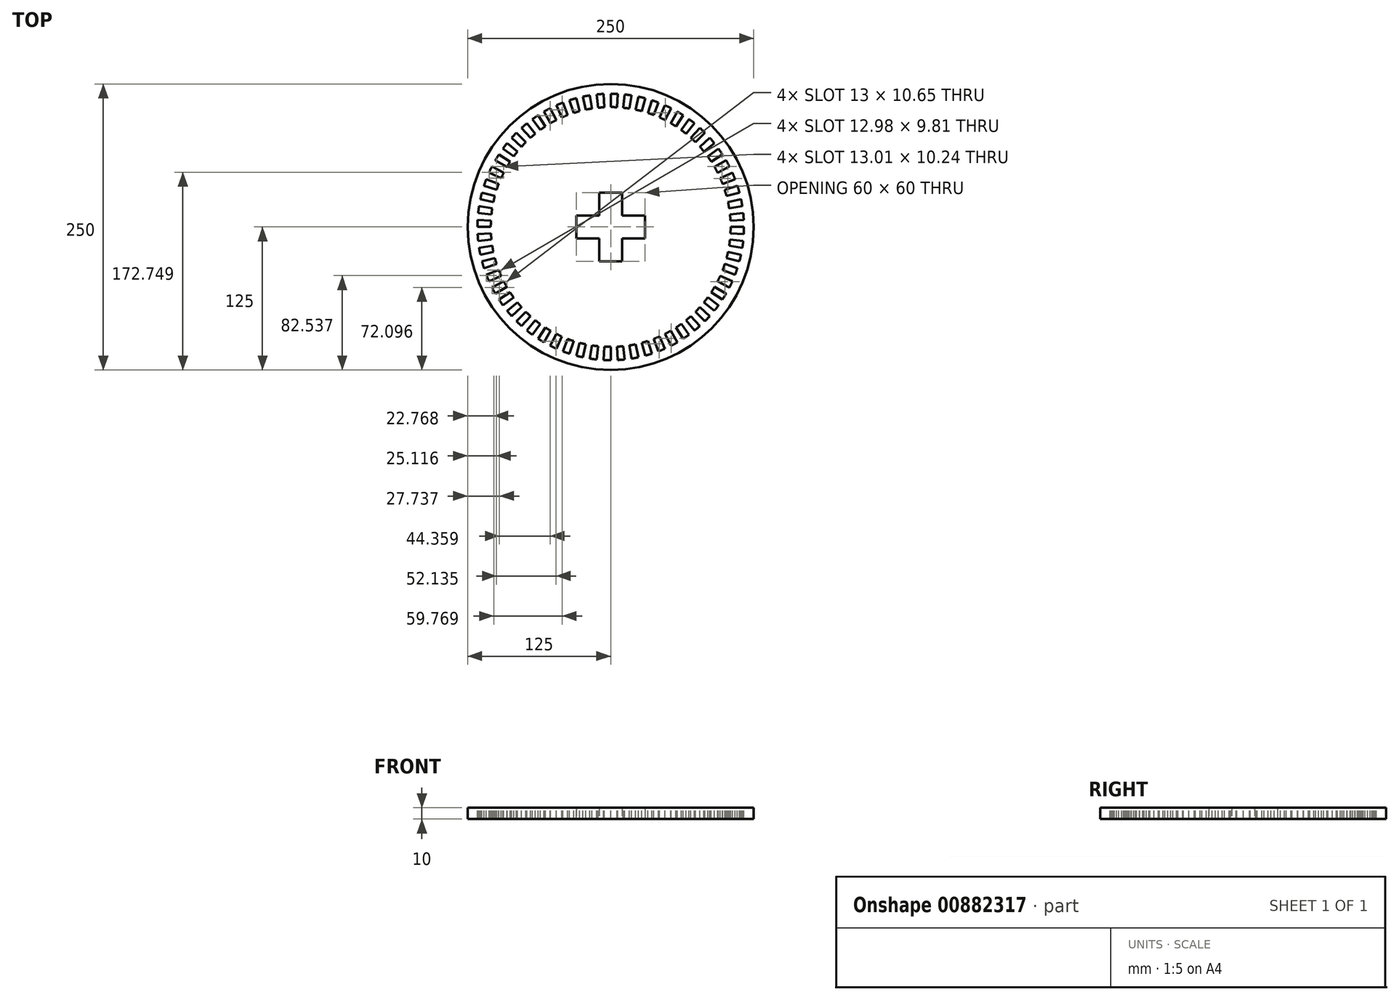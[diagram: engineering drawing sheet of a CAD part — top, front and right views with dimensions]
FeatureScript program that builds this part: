
annotation { "Feature Type Name" : "Feature", "Feature Type Description" : "" }
export const myFeature = defineFeature(function(context is Context, id is Id, definition is map)
    precondition{}
    {
        {
            var Q0;
            Q0=qCreatedBy(makeId("Top.planeOp"),FACE);
            var sketch = newSketch(context, id + "F0", { "sketchPlane" : qUnion([Q0])});
            skCircle(sketch, "E0", {"center": v(0, 0) * mm, "radius": 145 * mm});
            skArc(sketch, "E1", {"start": v(9.54, 136.41) * mm, "mid": v(4.77, 136.66) * mm, "end": v(0, 136.75) * mm});
            skArc(sketch, "E2", {"start": v(8, 114.55) * mm, "mid": v(4, 114.76) * mm, "end": v(0, 114.83) * mm});
            skLineSegment(sketch, "E3", {"start": v(0, 0) * mm, "end": v(0, 38.61) * mm, "construction": true});
            skLineSegment(sketch, "E4", {"start": v(0, 38.61) * mm, "end": v(0, 0) * mm, "construction": true});
            skLineSegment(sketch, "E5", {"start": v(0, 0) * mm, "end": v(-47.77, 0) * mm, "construction": true});
            skLineSegment(sketch, "E6", {"start": v(0, 30) * mm, "end": v(-10, 30) * mm});
            skLineSegment(sketch, "E7", {"start": v(-10, 30) * mm, "end": v(-10, 10) * mm});
            skLineSegment(sketch, "E8", {"start": v(-10, 10) * mm, "end": v(-30, 10) * mm});
            skLineSegment(sketch, "E9", {"start": v(-30, 10) * mm, "end": v(-30, 0) * mm});
            skLineSegment(sketch, "E10.MirrorCS", {"start": v(-30, -10) * mm, "end": v(-30, 0) * mm});
            skLineSegment(sketch, "E11.MirrorCS", {"start": v(-10, -10) * mm, "end": v(-30, -10) * mm});
            skLineSegment(sketch, "E12.MirrorCS", {"start": v(-10, -30) * mm, "end": v(-10, -10) * mm});
            skLineSegment(sketch, "E13.MirrorCS", {"start": v(0, -30) * mm, "end": v(-10, -30) * mm});
            skLineSegment(sketch, "E14.MirrorCS", {"start": v(0, 30) * mm, "end": v(10, 30) * mm});
            skLineSegment(sketch, "E15.MirrorCS", {"start": v(10, 30) * mm, "end": v(10, 10) * mm});
            skLineSegment(sketch, "E16.MirrorCS", {"start": v(10, 10) * mm, "end": v(30, 10) * mm});
            skLineSegment(sketch, "E17.MirrorCS", {"start": v(30, 10) * mm, "end": v(30, 0) * mm});
            skLineSegment(sketch, "E18.MirrorCS", {"start": v(30, -10) * mm, "end": v(30, 0) * mm});
            skLineSegment(sketch, "E19.MirrorCS", {"start": v(10, -10) * mm, "end": v(30, -10) * mm});
            skLineSegment(sketch, "E20.MirrorCS", {"start": v(0, -30) * mm, "end": v(10, -30) * mm});
            skLineSegment(sketch, "E21.MirrorCS", {"start": v(10, -30) * mm, "end": v(10, -10) * mm});
            skLineSegment(sketch, "E22", {"start": v(0, 114.83) * mm, "end": v(0, 136.75) * mm});
            skLineSegment(sketch, "E23", {"start": v(8, 114.55) * mm, "end": v(9.54, 136.41) * mm});
            skArc(sketch, "E24.1.0", {"start": v(-10, 114.4) * mm, "mid": v(-14, 113.98) * mm, "end": v(-17.96, 113.42) * mm});
            skLineSegment(sketch, "E24.1.1", {"start": v(-17.96, 113.42) * mm, "end": v(-21.4, 135.06) * mm});
            skArc(sketch, "E24.1.2", {"start": v(-11.92, 136.23) * mm, "mid": v(-16.67, 135.73) * mm, "end": v(-21.4, 135.06) * mm});
            skLineSegment(sketch, "E24.1.3", {"start": v(-10, 114.4) * mm, "end": v(-11.92, 136.23) * mm});
            skArc(sketch, "E24.2.0", {"start": v(-27.78, 111.42) * mm, "mid": v(-31.65, 110.39) * mm, "end": v(-35.49, 109.21) * mm});
            skLineSegment(sketch, "E24.2.1", {"start": v(-35.49, 109.21) * mm, "end": v(-42.26, 130.05) * mm});
            skArc(sketch, "E24.2.2", {"start": v(-33.08, 132.68) * mm, "mid": v(-37.7, 131.45) * mm, "end": v(-42.26, 130.05) * mm});
            skLineSegment(sketch, "E24.2.3", {"start": v(-27.78, 111.42) * mm, "end": v(-33.08, 132.68) * mm});
            skArc(sketch, "E24.3.0", {"start": v(-44.87, 105.7) * mm, "mid": v(-48.53, 104.07) * mm, "end": v(-52.13, 102.32) * mm});
            skLineSegment(sketch, "E24.3.1", {"start": v(-52.13, 102.32) * mm, "end": v(-62.08, 121.84) * mm});
            skArc(sketch, "E24.3.2", {"start": v(-53.43, 125.88) * mm, "mid": v(-57.8, 123.93) * mm, "end": v(-62.08, 121.84) * mm});
            skLineSegment(sketch, "E24.3.3", {"start": v(-44.87, 105.7) * mm, "end": v(-53.43, 125.88) * mm});
            skArc(sketch, "E24.4.0", {"start": v(-60.85, 97.38) * mm, "mid": v(-64.21, 95.2) * mm, "end": v(-67.5, 92.9) * mm});
            skLineSegment(sketch, "E24.4.1", {"start": v(-67.5, 92.9) * mm, "end": v(-80.38, 110.63) * mm});
            skArc(sketch, "E24.4.2", {"start": v(-72.47, 115.97) * mm, "mid": v(-76.47, 113.37) * mm, "end": v(-80.38, 110.63) * mm});
            skLineSegment(sketch, "E24.4.3", {"start": v(-60.85, 97.38) * mm, "end": v(-72.47, 115.97) * mm});
            skArc(sketch, "E24.5.0", {"start": v(-75.34, 86.67) * mm, "mid": v(-78.32, 83.98) * mm, "end": v(-81.2, 81.2) * mm});
            skLineSegment(sketch, "E24.5.1", {"start": v(-81.2, 81.2) * mm, "end": v(-96.7, 96.7) * mm});
            skArc(sketch, "E24.5.2", {"start": v(-89.71, 103.2) * mm, "mid": v(-93.26, 100.01) * mm, "end": v(-96.7, 96.7) * mm});
            skLineSegment(sketch, "E24.5.3", {"start": v(-75.34, 86.67) * mm, "end": v(-89.71, 103.2) * mm});
            skArc(sketch, "E24.6.0", {"start": v(-87.97, 73.81) * mm, "mid": v(-90.5, 70.7) * mm, "end": v(-92.9, 67.5) * mm});
            skLineSegment(sketch, "E24.6.1", {"start": v(-92.9, 67.5) * mm, "end": v(-110.63, 80.38) * mm});
            skArc(sketch, "E24.6.2", {"start": v(-104.75, 87.9) * mm, "mid": v(-107.76, 84.19) * mm, "end": v(-110.63, 80.38) * mm});
            skLineSegment(sketch, "E24.6.3", {"start": v(-87.97, 73.81) * mm, "end": v(-104.75, 87.9) * mm});
            skArc(sketch, "E24.7.0", {"start": v(-98.43, 59.14) * mm, "mid": v(-100.44, 55.67) * mm, "end": v(-102.32, 52.13) * mm});
            skLineSegment(sketch, "E24.7.1", {"start": v(-102.32, 52.13) * mm, "end": v(-121.84, 62.08) * mm});
            skArc(sketch, "E24.7.2", {"start": v(-117.22, 70.43) * mm, "mid": v(-119.6, 66.3) * mm, "end": v(-121.84, 62.08) * mm});
            skLineSegment(sketch, "E24.7.3", {"start": v(-98.43, 59.14) * mm, "end": v(-117.22, 70.43) * mm});
            skArc(sketch, "E24.8.0", {"start": v(-106.47, 43.02) * mm, "mid": v(-107.9, 39.28) * mm, "end": v(-109.21, 35.49) * mm});
            skLineSegment(sketch, "E24.8.1", {"start": v(-109.21, 35.49) * mm, "end": v(-130.05, 42.26) * mm});
            skArc(sketch, "E24.8.2", {"start": v(-126.79, 51.23) * mm, "mid": v(-128.5, 46.77) * mm, "end": v(-130.05, 42.26) * mm});
            skLineSegment(sketch, "E24.8.3", {"start": v(-106.47, 43.02) * mm, "end": v(-126.79, 51.23) * mm});
            skArc(sketch, "E24.9.0", {"start": v(-111.9, 25.83) * mm, "mid": v(-112.72, 21.91) * mm, "end": v(-113.42, 17.96) * mm});
            skLineSegment(sketch, "E24.9.1", {"start": v(-113.42, 17.96) * mm, "end": v(-135.06, 21.4) * mm});
            skArc(sketch, "E24.9.2", {"start": v(-133.24, 30.76) * mm, "mid": v(-134.23, 26.1) * mm, "end": v(-135.06, 21.4) * mm});
            skLineSegment(sketch, "E24.9.3", {"start": v(-111.9, 25.83) * mm, "end": v(-133.24, 30.76) * mm});
            skArc(sketch, "E24.10.0", {"start": v(-114.55, 8) * mm, "mid": v(-114.76, 4) * mm, "end": v(-114.83, 0) * mm});
            skLineSegment(sketch, "E24.10.1", {"start": v(-114.83, 0) * mm, "end": v(-136.75, 0) * mm});
            skArc(sketch, "E24.10.2", {"start": v(-136.41, 9.54) * mm, "mid": v(-136.66, 4.77) * mm, "end": v(-136.75, 0) * mm});
            skLineSegment(sketch, "E24.10.3", {"start": v(-114.55, 8) * mm, "end": v(-136.41, 9.54) * mm});
            skArc(sketch, "E24.11.0", {"start": v(-114.4, -10) * mm, "mid": v(-113.98, -14) * mm, "end": v(-113.42, -17.96) * mm});
            skLineSegment(sketch, "E24.11.1", {"start": v(-113.42, -17.96) * mm, "end": v(-135.06, -21.4) * mm});
            skArc(sketch, "E24.11.2", {"start": v(-136.23, -11.92) * mm, "mid": v(-135.73, -16.67) * mm, "end": v(-135.06, -21.4) * mm});
            skLineSegment(sketch, "E24.11.3", {"start": v(-114.4, -10) * mm, "end": v(-136.23, -11.92) * mm});
            skArc(sketch, "E24.12.0", {"start": v(-111.42, -27.78) * mm, "mid": v(-110.39, -31.65) * mm, "end": v(-109.21, -35.49) * mm});
            skLineSegment(sketch, "E24.12.1", {"start": v(-109.21, -35.49) * mm, "end": v(-130.05, -42.26) * mm});
            skArc(sketch, "E24.12.2", {"start": v(-132.68, -33.08) * mm, "mid": v(-131.45, -37.7) * mm, "end": v(-130.05, -42.26) * mm});
            skLineSegment(sketch, "E24.12.3", {"start": v(-111.42, -27.78) * mm, "end": v(-132.68, -33.08) * mm});
            skArc(sketch, "E24.13.0", {"start": v(-105.7, -44.87) * mm, "mid": v(-104.07, -48.53) * mm, "end": v(-102.32, -52.13) * mm});
            skLineSegment(sketch, "E24.13.1", {"start": v(-102.32, -52.13) * mm, "end": v(-121.84, -62.08) * mm});
            skArc(sketch, "E24.13.2", {"start": v(-125.88, -53.43) * mm, "mid": v(-123.93, -57.8) * mm, "end": v(-121.84, -62.08) * mm});
            skLineSegment(sketch, "E24.13.3", {"start": v(-105.7, -44.87) * mm, "end": v(-125.88, -53.43) * mm});
            skArc(sketch, "E24.14.0", {"start": v(-97.38, -60.85) * mm, "mid": v(-95.2, -64.21) * mm, "end": v(-92.9, -67.5) * mm});
            skLineSegment(sketch, "E24.14.1", {"start": v(-92.9, -67.5) * mm, "end": v(-110.63, -80.38) * mm});
            skArc(sketch, "E24.14.2", {"start": v(-115.97, -72.47) * mm, "mid": v(-113.37, -76.47) * mm, "end": v(-110.63, -80.38) * mm});
            skLineSegment(sketch, "E24.14.3", {"start": v(-97.38, -60.85) * mm, "end": v(-115.97, -72.47) * mm});
            skArc(sketch, "E24.15.0", {"start": v(-86.67, -75.34) * mm, "mid": v(-83.98, -78.32) * mm, "end": v(-81.2, -81.2) * mm});
            skLineSegment(sketch, "E24.15.1", {"start": v(-81.2, -81.2) * mm, "end": v(-96.7, -96.7) * mm});
            skArc(sketch, "E24.15.2", {"start": v(-103.2, -89.71) * mm, "mid": v(-100.01, -93.26) * mm, "end": v(-96.7, -96.7) * mm});
            skLineSegment(sketch, "E24.15.3", {"start": v(-86.67, -75.34) * mm, "end": v(-103.2, -89.71) * mm});
            skArc(sketch, "E24.16.0", {"start": v(-73.81, -87.97) * mm, "mid": v(-70.7, -90.5) * mm, "end": v(-67.5, -92.9) * mm});
            skLineSegment(sketch, "E24.16.1", {"start": v(-67.5, -92.9) * mm, "end": v(-80.38, -110.63) * mm});
            skArc(sketch, "E24.16.2", {"start": v(-87.9, -104.75) * mm, "mid": v(-84.19, -107.76) * mm, "end": v(-80.38, -110.63) * mm});
            skLineSegment(sketch, "E24.16.3", {"start": v(-73.81, -87.97) * mm, "end": v(-87.9, -104.75) * mm});
            skArc(sketch, "E24.17.0", {"start": v(-59.14, -98.43) * mm, "mid": v(-55.67, -100.44) * mm, "end": v(-52.13, -102.32) * mm});
            skLineSegment(sketch, "E24.17.1", {"start": v(-52.13, -102.32) * mm, "end": v(-62.08, -121.84) * mm});
            skArc(sketch, "E24.17.2", {"start": v(-70.43, -117.22) * mm, "mid": v(-66.3, -119.6) * mm, "end": v(-62.08, -121.84) * mm});
            skLineSegment(sketch, "E24.17.3", {"start": v(-59.14, -98.43) * mm, "end": v(-70.43, -117.22) * mm});
            skArc(sketch, "E24.18.0", {"start": v(-43.02, -106.47) * mm, "mid": v(-39.28, -107.9) * mm, "end": v(-35.49, -109.21) * mm});
            skLineSegment(sketch, "E24.18.1", {"start": v(-35.49, -109.21) * mm, "end": v(-42.26, -130.05) * mm});
            skArc(sketch, "E24.18.2", {"start": v(-51.23, -126.79) * mm, "mid": v(-46.77, -128.5) * mm, "end": v(-42.26, -130.05) * mm});
            skLineSegment(sketch, "E24.18.3", {"start": v(-43.02, -106.47) * mm, "end": v(-51.23, -126.79) * mm});
            skArc(sketch, "E24.19.0", {"start": v(-25.83, -111.9) * mm, "mid": v(-21.91, -112.72) * mm, "end": v(-17.96, -113.42) * mm});
            skLineSegment(sketch, "E24.19.1", {"start": v(-17.96, -113.42) * mm, "end": v(-21.4, -135.06) * mm});
            skArc(sketch, "E24.19.2", {"start": v(-30.76, -133.24) * mm, "mid": v(-26.1, -134.23) * mm, "end": v(-21.4, -135.06) * mm});
            skLineSegment(sketch, "E24.19.3", {"start": v(-25.83, -111.9) * mm, "end": v(-30.76, -133.24) * mm});
            skArc(sketch, "E24.20.0", {"start": v(-8, -114.55) * mm, "mid": v(-4, -114.76) * mm, "end": v(0, -114.83) * mm});
            skLineSegment(sketch, "E24.20.1", {"start": v(0, -114.83) * mm, "end": v(0, -136.75) * mm});
            skArc(sketch, "E24.20.2", {"start": v(-9.54, -136.41) * mm, "mid": v(-4.77, -136.66) * mm, "end": v(0, -136.75) * mm});
            skLineSegment(sketch, "E24.20.3", {"start": v(-8, -114.55) * mm, "end": v(-9.54, -136.41) * mm});
            skArc(sketch, "E24.21.0", {"start": v(10, -114.4) * mm, "mid": v(14, -113.98) * mm, "end": v(17.96, -113.42) * mm});
            skLineSegment(sketch, "E24.21.1", {"start": v(17.96, -113.42) * mm, "end": v(21.4, -135.06) * mm});
            skArc(sketch, "E24.21.2", {"start": v(11.92, -136.23) * mm, "mid": v(16.67, -135.73) * mm, "end": v(21.4, -135.06) * mm});
            skLineSegment(sketch, "E24.21.3", {"start": v(10, -114.4) * mm, "end": v(11.92, -136.23) * mm});
            skArc(sketch, "E24.22.0", {"start": v(27.78, -111.42) * mm, "mid": v(31.65, -110.39) * mm, "end": v(35.49, -109.21) * mm});
            skLineSegment(sketch, "E24.22.1", {"start": v(35.49, -109.21) * mm, "end": v(42.26, -130.05) * mm});
            skArc(sketch, "E24.22.2", {"start": v(33.08, -132.68) * mm, "mid": v(37.7, -131.45) * mm, "end": v(42.26, -130.05) * mm});
            skLineSegment(sketch, "E24.22.3", {"start": v(27.78, -111.42) * mm, "end": v(33.08, -132.68) * mm});
            skArc(sketch, "E24.23.0", {"start": v(44.87, -105.7) * mm, "mid": v(48.53, -104.07) * mm, "end": v(52.13, -102.32) * mm});
            skLineSegment(sketch, "E24.23.1", {"start": v(52.13, -102.32) * mm, "end": v(62.08, -121.84) * mm});
            skArc(sketch, "E24.23.2", {"start": v(53.43, -125.88) * mm, "mid": v(57.8, -123.93) * mm, "end": v(62.08, -121.84) * mm});
            skLineSegment(sketch, "E24.23.3", {"start": v(44.87, -105.7) * mm, "end": v(53.43, -125.88) * mm});
            skArc(sketch, "E24.24.0", {"start": v(60.85, -97.38) * mm, "mid": v(64.21, -95.2) * mm, "end": v(67.5, -92.9) * mm});
            skLineSegment(sketch, "E24.24.1", {"start": v(67.5, -92.9) * mm, "end": v(80.38, -110.63) * mm});
            skArc(sketch, "E24.24.2", {"start": v(72.47, -115.97) * mm, "mid": v(76.47, -113.37) * mm, "end": v(80.38, -110.63) * mm});
            skLineSegment(sketch, "E24.24.3", {"start": v(60.85, -97.38) * mm, "end": v(72.47, -115.97) * mm});
            skArc(sketch, "E24.25.0", {"start": v(75.34, -86.67) * mm, "mid": v(78.32, -83.98) * mm, "end": v(81.2, -81.2) * mm});
            skLineSegment(sketch, "E24.25.1", {"start": v(81.2, -81.2) * mm, "end": v(96.7, -96.7) * mm});
            skArc(sketch, "E24.25.2", {"start": v(89.71, -103.2) * mm, "mid": v(93.26, -100.01) * mm, "end": v(96.7, -96.7) * mm});
            skLineSegment(sketch, "E24.25.3", {"start": v(75.34, -86.67) * mm, "end": v(89.71, -103.2) * mm});
            skArc(sketch, "E24.26.0", {"start": v(87.97, -73.81) * mm, "mid": v(90.5, -70.7) * mm, "end": v(92.9, -67.5) * mm});
            skLineSegment(sketch, "E24.26.1", {"start": v(92.9, -67.5) * mm, "end": v(110.63, -80.38) * mm});
            skArc(sketch, "E24.26.2", {"start": v(104.75, -87.9) * mm, "mid": v(107.76, -84.19) * mm, "end": v(110.63, -80.38) * mm});
            skLineSegment(sketch, "E24.26.3", {"start": v(87.97, -73.81) * mm, "end": v(104.75, -87.9) * mm});
            skArc(sketch, "E24.27.0", {"start": v(98.43, -59.14) * mm, "mid": v(100.44, -55.67) * mm, "end": v(102.32, -52.13) * mm});
            skLineSegment(sketch, "E24.27.1", {"start": v(102.32, -52.13) * mm, "end": v(121.84, -62.08) * mm});
            skArc(sketch, "E24.27.2", {"start": v(117.22, -70.43) * mm, "mid": v(119.6, -66.3) * mm, "end": v(121.84, -62.08) * mm});
            skLineSegment(sketch, "E24.27.3", {"start": v(98.43, -59.14) * mm, "end": v(117.22, -70.43) * mm});
            skArc(sketch, "E24.28.0", {"start": v(106.47, -43.02) * mm, "mid": v(107.9, -39.28) * mm, "end": v(109.21, -35.49) * mm});
            skLineSegment(sketch, "E24.28.1", {"start": v(109.21, -35.49) * mm, "end": v(130.05, -42.26) * mm});
            skArc(sketch, "E24.28.2", {"start": v(126.79, -51.23) * mm, "mid": v(128.5, -46.77) * mm, "end": v(130.05, -42.26) * mm});
            skLineSegment(sketch, "E24.28.3", {"start": v(106.47, -43.02) * mm, "end": v(126.79, -51.23) * mm});
            skArc(sketch, "E24.29.0", {"start": v(111.9, -25.83) * mm, "mid": v(112.72, -21.91) * mm, "end": v(113.42, -17.96) * mm});
            skLineSegment(sketch, "E24.29.1", {"start": v(113.42, -17.96) * mm, "end": v(135.06, -21.4) * mm});
            skArc(sketch, "E24.29.2", {"start": v(133.24, -30.76) * mm, "mid": v(134.23, -26.1) * mm, "end": v(135.06, -21.4) * mm});
            skLineSegment(sketch, "E24.29.3", {"start": v(111.9, -25.83) * mm, "end": v(133.24, -30.76) * mm});
            skArc(sketch, "E24.30.0", {"start": v(114.55, -8) * mm, "mid": v(114.76, -4) * mm, "end": v(114.83, 0) * mm});
            skLineSegment(sketch, "E24.30.1", {"start": v(114.83, 0) * mm, "end": v(136.75, 0) * mm});
            skArc(sketch, "E24.30.2", {"start": v(136.41, -9.54) * mm, "mid": v(136.66, -4.77) * mm, "end": v(136.75, 0) * mm});
            skLineSegment(sketch, "E24.30.3", {"start": v(114.55, -8) * mm, "end": v(136.41, -9.54) * mm});
            skArc(sketch, "E24.31.0", {"start": v(114.4, 10) * mm, "mid": v(113.98, 14) * mm, "end": v(113.42, 17.96) * mm});
            skLineSegment(sketch, "E24.31.1", {"start": v(113.42, 17.96) * mm, "end": v(135.06, 21.4) * mm});
            skArc(sketch, "E24.31.2", {"start": v(136.23, 11.92) * mm, "mid": v(135.73, 16.67) * mm, "end": v(135.06, 21.4) * mm});
            skLineSegment(sketch, "E24.31.3", {"start": v(114.4, 10) * mm, "end": v(136.23, 11.92) * mm});
            skArc(sketch, "E24.32.0", {"start": v(111.42, 27.78) * mm, "mid": v(110.39, 31.65) * mm, "end": v(109.21, 35.49) * mm});
            skLineSegment(sketch, "E24.32.1", {"start": v(109.21, 35.49) * mm, "end": v(130.05, 42.26) * mm});
            skArc(sketch, "E24.32.2", {"start": v(132.68, 33.08) * mm, "mid": v(131.45, 37.7) * mm, "end": v(130.05, 42.26) * mm});
            skLineSegment(sketch, "E24.32.3", {"start": v(111.42, 27.78) * mm, "end": v(132.68, 33.08) * mm});
            skArc(sketch, "E24.33.0", {"start": v(105.7, 44.87) * mm, "mid": v(104.07, 48.53) * mm, "end": v(102.32, 52.13) * mm});
            skLineSegment(sketch, "E24.33.1", {"start": v(102.32, 52.13) * mm, "end": v(121.84, 62.08) * mm});
            skArc(sketch, "E24.33.2", {"start": v(125.88, 53.43) * mm, "mid": v(123.93, 57.8) * mm, "end": v(121.84, 62.08) * mm});
            skLineSegment(sketch, "E24.33.3", {"start": v(105.7, 44.87) * mm, "end": v(125.88, 53.43) * mm});
            skArc(sketch, "E24.34.0", {"start": v(97.38, 60.85) * mm, "mid": v(95.2, 64.21) * mm, "end": v(92.9, 67.5) * mm});
            skLineSegment(sketch, "E24.34.1", {"start": v(92.9, 67.5) * mm, "end": v(110.63, 80.38) * mm});
            skArc(sketch, "E24.34.2", {"start": v(115.97, 72.47) * mm, "mid": v(113.37, 76.47) * mm, "end": v(110.63, 80.38) * mm});
            skLineSegment(sketch, "E24.34.3", {"start": v(97.38, 60.85) * mm, "end": v(115.97, 72.47) * mm});
            skArc(sketch, "E24.35.0", {"start": v(86.67, 75.34) * mm, "mid": v(83.98, 78.32) * mm, "end": v(81.2, 81.2) * mm});
            skLineSegment(sketch, "E24.35.1", {"start": v(81.2, 81.2) * mm, "end": v(96.7, 96.7) * mm});
            skArc(sketch, "E24.35.2", {"start": v(103.2, 89.71) * mm, "mid": v(100.01, 93.26) * mm, "end": v(96.7, 96.7) * mm});
            skLineSegment(sketch, "E24.35.3", {"start": v(86.67, 75.34) * mm, "end": v(103.2, 89.71) * mm});
            skArc(sketch, "E24.36.0", {"start": v(73.81, 87.97) * mm, "mid": v(70.7, 90.5) * mm, "end": v(67.5, 92.9) * mm});
            skLineSegment(sketch, "E24.36.1", {"start": v(67.5, 92.9) * mm, "end": v(80.38, 110.63) * mm});
            skArc(sketch, "E24.36.2", {"start": v(87.9, 104.75) * mm, "mid": v(84.19, 107.76) * mm, "end": v(80.38, 110.63) * mm});
            skLineSegment(sketch, "E24.36.3", {"start": v(73.81, 87.97) * mm, "end": v(87.9, 104.75) * mm});
            skArc(sketch, "E24.37.0", {"start": v(59.14, 98.43) * mm, "mid": v(55.67, 100.44) * mm, "end": v(52.13, 102.32) * mm});
            skLineSegment(sketch, "E24.37.1", {"start": v(52.13, 102.32) * mm, "end": v(62.08, 121.84) * mm});
            skArc(sketch, "E24.37.2", {"start": v(70.43, 117.22) * mm, "mid": v(66.3, 119.6) * mm, "end": v(62.08, 121.84) * mm});
            skLineSegment(sketch, "E24.37.3", {"start": v(59.14, 98.43) * mm, "end": v(70.43, 117.22) * mm});
            skArc(sketch, "E24.38.0", {"start": v(43.02, 106.47) * mm, "mid": v(39.28, 107.9) * mm, "end": v(35.49, 109.21) * mm});
            skLineSegment(sketch, "E24.38.1", {"start": v(35.49, 109.21) * mm, "end": v(42.26, 130.05) * mm});
            skArc(sketch, "E24.38.2", {"start": v(51.23, 126.79) * mm, "mid": v(46.77, 128.5) * mm, "end": v(42.26, 130.05) * mm});
            skLineSegment(sketch, "E24.38.3", {"start": v(43.02, 106.47) * mm, "end": v(51.23, 126.79) * mm});
            skArc(sketch, "E24.39.0", {"start": v(25.83, 111.9) * mm, "mid": v(21.91, 112.72) * mm, "end": v(17.96, 113.42) * mm});
            skLineSegment(sketch, "E24.39.1", {"start": v(17.96, 113.42) * mm, "end": v(21.4, 135.06) * mm});
            skArc(sketch, "E24.39.2", {"start": v(30.76, 133.24) * mm, "mid": v(26.1, 134.23) * mm, "end": v(21.4, 135.06) * mm});
            skLineSegment(sketch, "E24.39.3", {"start": v(25.83, 111.9) * mm, "end": v(30.76, 133.24) * mm});
            skCircle(sketch, "E25", {"center": v(0, 0) * mm, "radius": 50 * mm});
            skSolve(sketch);
        }
        {
            var Q0;
            Q0=makeQuery(id+"F0.imprint","IMPRINT",FACE,{"disambiguationData":[TD([[makeQuery(id+"F0.imprint","IMPRINT",EDGE,{"derivedFrom":sQuery(id+"F0.wireOp",EDGE,"E6")}),-1.0]])]});
            extrude(context, id + "F1", {"entities" : qUnion([Q0]), "depth" : 10 * mm, "offsetDistance" : 25 * mm});
        }
        {
            var Q0;
            Q0=makeQuery(id+"F1.opExtrude","CAP_FACE",FACE,{"disambiguationData":[OSD([sQuery(id+"F0.wireOp",EDGE,"E6"),sQuery(id+"F0.wireOp",EDGE,"E7"),sQuery(id+"F0.wireOp",EDGE,"E8"),sQuery(id+"F0.wireOp",EDGE,"E9"),sQuery(id+"F0.wireOp",EDGE,"E10.MirrorCS"),sQuery(id+"F0.wireOp",EDGE,"E11.MirrorCS"),sQuery(id+"F0.wireOp",EDGE,"E12.MirrorCS"),sQuery(id+"F0.wireOp",EDGE,"E13.MirrorCS"),sQuery(id+"F0.wireOp",EDGE,"E14.MirrorCS"),sQuery(id+"F0.wireOp",EDGE,"E15.MirrorCS"),sQuery(id+"F0.wireOp",EDGE,"E16.MirrorCS"),sQuery(id+"F0.wireOp",EDGE,"E17.MirrorCS"),sQuery(id+"F0.wireOp",EDGE,"E18.MirrorCS"),sQuery(id+"F0.wireOp",EDGE,"E19.MirrorCS"),sQuery(id+"F0.wireOp",EDGE,"E20.MirrorCS"),sQuery(id+"F0.wireOp",EDGE,"E21.MirrorCS"),sQuery(id+"F0.wireOp",EDGE,"E25")])],"isStart":false});
            var sketch = newSketch(context, id + "F2", { "sketchPlane" : qUnion([Q0])});
            skCircle(sketch, "E26", {"center": v(0, 0) * mm, "radius": 125 * mm});
            skCircle(sketch, "E27", {"center": v(0, 0) * mm, "radius": 40.45 * mm});
            skSolve(sketch);
        }
        {
            var Q0;
            Q0=qSketchRegion(id+"F2",true);
            extrude(context, id + "F3", {"entities" : qUnion([Q0]), "operationType" : NewBodyOperationType.ADD, "oppositeDirection" : true, "depth" : 10 * mm, "offsetDistance" : 25 * mm});
        }
        {
            var Q0;
            Q0=makeQuery(id+"F3.boolean.opBoolean","MERGE",FACE,{"derivedFrom":[makeQuery(id+"F1.opExtrude","CAP_FACE",FACE,{"disambiguationData":[OSD([sQuery(id+"F0.wireOp",EDGE,"E6"),sQuery(id+"F0.wireOp",EDGE,"E7"),sQuery(id+"F0.wireOp",EDGE,"E8"),sQuery(id+"F0.wireOp",EDGE,"E9"),sQuery(id+"F0.wireOp",EDGE,"E10.MirrorCS"),sQuery(id+"F0.wireOp",EDGE,"E11.MirrorCS"),sQuery(id+"F0.wireOp",EDGE,"E12.MirrorCS"),sQuery(id+"F0.wireOp",EDGE,"E13.MirrorCS"),sQuery(id+"F0.wireOp",EDGE,"E14.MirrorCS"),sQuery(id+"F0.wireOp",EDGE,"E15.MirrorCS"),sQuery(id+"F0.wireOp",EDGE,"E16.MirrorCS"),sQuery(id+"F0.wireOp",EDGE,"E17.MirrorCS"),sQuery(id+"F0.wireOp",EDGE,"E18.MirrorCS"),sQuery(id+"F0.wireOp",EDGE,"E19.MirrorCS"),sQuery(id+"F0.wireOp",EDGE,"E20.MirrorCS"),sQuery(id+"F0.wireOp",EDGE,"E21.MirrorCS"),sQuery(id+"F0.wireOp",EDGE,"E25")])],"isStart":false}),makeQuery(id+"F3.opExtrude","CAP_FACE",FACE,{"disambiguationData":[OSD([sQuery(id+"F2.wireOp",EDGE,"E26"),sQuery(id+"F2.wireOp",EDGE,"E27")])],"isStart":true})]});
            var sketch = newSketch(context, id + "F4", { "sketchPlane" : qUnion([Q0])});
            skLineSegment(sketch, "E28", {"start": v(0, 104.8) * mm, "end": v(0, 116.46) * mm});
            skLineSegment(sketch, "E29", {"start": v(0, 116.46) * mm, "end": v(0, 104.8) * mm});
            skLineSegment(sketch, "E30", {"start": v(5.48, 104.66) * mm, "end": v(6.1, 116.3) * mm});
            skArc(sketch, "E31", {"start": v(6.1, 116.3) * mm, "mid": v(3.05, 116.42) * mm, "end": v(0, 116.46) * mm});
            skArc(sketch, "E32", {"start": v(5.48, 104.66) * mm, "mid": v(2.74, 104.77) * mm, "end": v(0, 104.8) * mm});
            skArc(sketch, "E33.1.0", {"start": v(-5.48, 104.66) * mm, "mid": v(-8.22, 104.48) * mm, "end": v(-10.95, 104.23) * mm});
            skLineSegment(sketch, "E33.1.1", {"start": v(-12.17, 115.82) * mm, "end": v(-10.95, 104.23) * mm});
            skArc(sketch, "E33.1.2", {"start": v(-6.1, 116.3) * mm, "mid": v(-9.14, 116.1) * mm, "end": v(-12.17, 115.82) * mm});
            skLineSegment(sketch, "E33.1.3", {"start": v(-5.48, 104.66) * mm, "end": v(-6.1, 116.3) * mm});
            skArc(sketch, "E33.2.0", {"start": v(-16.4, 103.51) * mm, "mid": v(-19.1, 103.05) * mm, "end": v(-21.79, 102.51) * mm});
            skLineSegment(sketch, "E33.2.1", {"start": v(-24.21, 113.91) * mm, "end": v(-21.79, 102.51) * mm});
            skArc(sketch, "E33.2.2", {"start": v(-18.22, 115.02) * mm, "mid": v(-21.22, 114.5) * mm, "end": v(-24.21, 113.91) * mm});
            skLineSegment(sketch, "E33.2.3", {"start": v(-16.4, 103.51) * mm, "end": v(-18.22, 115.02) * mm});
            skArc(sketch, "E33.3.0", {"start": v(-27.12, 101.23) * mm, "mid": v(-29.77, 100.49) * mm, "end": v(-32.39, 99.67) * mm});
            skLineSegment(sketch, "E33.3.1", {"start": v(-35.99, 110.76) * mm, "end": v(-32.39, 99.67) * mm});
            skArc(sketch, "E33.3.2", {"start": v(-30.14, 112.49) * mm, "mid": v(-33.08, 111.66) * mm, "end": v(-35.99, 110.76) * mm});
            skLineSegment(sketch, "E33.3.3", {"start": v(-27.12, 101.23) * mm, "end": v(-30.14, 112.49) * mm});
            skArc(sketch, "E33.4.0", {"start": v(-37.56, 97.84) * mm, "mid": v(-40.1, 96.83) * mm, "end": v(-42.63, 95.74) * mm});
            skLineSegment(sketch, "E33.4.1", {"start": v(-47.37, 106.39) * mm, "end": v(-42.63, 95.74) * mm});
            skArc(sketch, "E33.4.2", {"start": v(-41.73, 108.72) * mm, "mid": v(-44.57, 107.6) * mm, "end": v(-47.37, 106.39) * mm});
            skLineSegment(sketch, "E33.4.3", {"start": v(-37.56, 97.84) * mm, "end": v(-41.73, 108.72) * mm});
            skArc(sketch, "E33.5.0", {"start": v(-47.58, 93.38) * mm, "mid": v(-50, 92.1) * mm, "end": v(-52.4, 90.76) * mm});
            skLineSegment(sketch, "E33.5.1", {"start": v(-58.23, 100.85) * mm, "end": v(-52.4, 90.76) * mm});
            skArc(sketch, "E33.5.2", {"start": v(-52.87, 103.76) * mm, "mid": v(-55.57, 102.34) * mm, "end": v(-58.23, 100.85) * mm});
            skLineSegment(sketch, "E33.5.3", {"start": v(-47.58, 93.38) * mm, "end": v(-52.87, 103.76) * mm});
            skArc(sketch, "E33.6.0", {"start": v(-57.08, 87.9) * mm, "mid": v(-59.36, 86.37) * mm, "end": v(-61.6, 84.79) * mm});
            skLineSegment(sketch, "E33.6.1", {"start": v(-68.45, 94.22) * mm, "end": v(-61.6, 84.79) * mm});
            skArc(sketch, "E33.6.2", {"start": v(-63.43, 97.67) * mm, "mid": v(-65.96, 95.97) * mm, "end": v(-68.45, 94.22) * mm});
            skLineSegment(sketch, "E33.6.3", {"start": v(-57.08, 87.9) * mm, "end": v(-63.43, 97.67) * mm});
            skArc(sketch, "E33.7.0", {"start": v(-65.95, 81.45) * mm, "mid": v(-68.06, 79.7) * mm, "end": v(-70.13, 77.88) * mm});
            skLineSegment(sketch, "E33.7.1", {"start": v(-77.92, 86.54) * mm, "end": v(-70.13, 77.88) * mm});
            skArc(sketch, "E33.7.2", {"start": v(-73.29, 90.5) * mm, "mid": v(-75.63, 88.55) * mm, "end": v(-77.92, 86.54) * mm});
            skLineSegment(sketch, "E33.7.3", {"start": v(-65.95, 81.45) * mm, "end": v(-73.29, 90.5) * mm});
            skArc(sketch, "E33.8.0", {"start": v(-74.1, 74.1) * mm, "mid": v(-76.02, 72.14) * mm, "end": v(-77.88, 70.13) * mm});
            skLineSegment(sketch, "E33.8.1", {"start": v(-86.54, 77.92) * mm, "end": v(-77.88, 70.13) * mm});
            skArc(sketch, "E33.8.2", {"start": v(-82.35, 82.35) * mm, "mid": v(-84.47, 80.16) * mm, "end": v(-86.54, 77.92) * mm});
            skLineSegment(sketch, "E33.8.3", {"start": v(-74.1, 74.1) * mm, "end": v(-82.35, 82.35) * mm});
            skArc(sketch, "E33.9.0", {"start": v(-81.45, 65.95) * mm, "mid": v(-83.15, 63.8) * mm, "end": v(-84.79, 61.6) * mm});
            skLineSegment(sketch, "E33.9.1", {"start": v(-94.22, 68.45) * mm, "end": v(-84.79, 61.6) * mm});
            skArc(sketch, "E33.9.2", {"start": v(-90.5, 73.29) * mm, "mid": v(-92.4, 70.9) * mm, "end": v(-94.22, 68.45) * mm});
            skLineSegment(sketch, "E33.9.3", {"start": v(-81.45, 65.95) * mm, "end": v(-90.5, 73.29) * mm});
            skArc(sketch, "E33.10.0", {"start": v(-87.9, 57.08) * mm, "mid": v(-89.36, 54.76) * mm, "end": v(-90.76, 52.4) * mm});
            skLineSegment(sketch, "E33.10.1", {"start": v(-100.85, 58.23) * mm, "end": v(-90.76, 52.4) * mm});
            skArc(sketch, "E33.10.2", {"start": v(-97.67, 63.43) * mm, "mid": v(-99.3, 60.85) * mm, "end": v(-100.85, 58.23) * mm});
            skLineSegment(sketch, "E33.10.3", {"start": v(-87.9, 57.08) * mm, "end": v(-97.67, 63.43) * mm});
            skArc(sketch, "E33.11.0", {"start": v(-93.38, 47.58) * mm, "mid": v(-94.6, 45.12) * mm, "end": v(-95.74, 42.63) * mm});
            skLineSegment(sketch, "E33.11.1", {"start": v(-106.39, 47.37) * mm, "end": v(-95.74, 42.63) * mm});
            skArc(sketch, "E33.11.2", {"start": v(-103.76, 52.87) * mm, "mid": v(-105.11, 50.14) * mm, "end": v(-106.39, 47.37) * mm});
            skLineSegment(sketch, "E33.11.3", {"start": v(-93.38, 47.58) * mm, "end": v(-103.76, 52.87) * mm});
            skArc(sketch, "E33.12.0", {"start": v(-97.84, 37.56) * mm, "mid": v(-98.8, 34.98) * mm, "end": v(-99.67, 32.39) * mm});
            skLineSegment(sketch, "E33.12.1", {"start": v(-110.76, 35.99) * mm, "end": v(-99.67, 32.39) * mm});
            skArc(sketch, "E33.12.2", {"start": v(-108.72, 41.73) * mm, "mid": v(-109.78, 38.87) * mm, "end": v(-110.76, 35.99) * mm});
            skLineSegment(sketch, "E33.12.3", {"start": v(-97.84, 37.56) * mm, "end": v(-108.72, 41.73) * mm});
            skArc(sketch, "E33.13.0", {"start": v(-101.23, 27.12) * mm, "mid": v(-101.9, 24.47) * mm, "end": v(-102.51, 21.79) * mm});
            skLineSegment(sketch, "E33.13.1", {"start": v(-113.91, 24.21) * mm, "end": v(-102.51, 21.79) * mm});
            skArc(sketch, "E33.13.2", {"start": v(-112.49, 30.14) * mm, "mid": v(-113.24, 27.19) * mm, "end": v(-113.91, 24.21) * mm});
            skLineSegment(sketch, "E33.13.3", {"start": v(-101.23, 27.12) * mm, "end": v(-112.49, 30.14) * mm});
            skArc(sketch, "E33.14.0", {"start": v(-103.51, 16.4) * mm, "mid": v(-103.9, 13.68) * mm, "end": v(-104.23, 10.95) * mm});
            skLineSegment(sketch, "E33.14.1", {"start": v(-115.82, 12.17) * mm, "end": v(-104.23, 10.95) * mm});
            skArc(sketch, "E33.14.2", {"start": v(-115.02, 18.22) * mm, "mid": v(-115.46, 15.2) * mm, "end": v(-115.82, 12.17) * mm});
            skLineSegment(sketch, "E33.14.3", {"start": v(-103.51, 16.4) * mm, "end": v(-115.02, 18.22) * mm});
            skArc(sketch, "E33.15.0", {"start": v(-104.66, 5.48) * mm, "mid": v(-104.77, 2.74) * mm, "end": v(-104.8, 0) * mm});
            skLineSegment(sketch, "E33.15.1", {"start": v(-116.46, 0) * mm, "end": v(-104.8, 0) * mm});
            skArc(sketch, "E33.15.2", {"start": v(-116.3, 6.1) * mm, "mid": v(-116.42, 3.05) * mm, "end": v(-116.46, 0) * mm});
            skLineSegment(sketch, "E33.15.3", {"start": v(-104.66, 5.48) * mm, "end": v(-116.3, 6.1) * mm});
            skArc(sketch, "E33.16.0", {"start": v(-104.66, -5.48) * mm, "mid": v(-104.48, -8.22) * mm, "end": v(-104.23, -10.95) * mm});
            skLineSegment(sketch, "E33.16.1", {"start": v(-115.82, -12.17) * mm, "end": v(-104.23, -10.95) * mm});
            skArc(sketch, "E33.16.2", {"start": v(-116.3, -6.1) * mm, "mid": v(-116.1, -9.14) * mm, "end": v(-115.82, -12.17) * mm});
            skLineSegment(sketch, "E33.16.3", {"start": v(-104.66, -5.48) * mm, "end": v(-116.3, -6.1) * mm});
            skArc(sketch, "E33.17.0", {"start": v(-103.51, -16.4) * mm, "mid": v(-103.05, -19.1) * mm, "end": v(-102.51, -21.79) * mm});
            skLineSegment(sketch, "E33.17.1", {"start": v(-113.91, -24.21) * mm, "end": v(-102.51, -21.79) * mm});
            skArc(sketch, "E33.17.2", {"start": v(-115.02, -18.22) * mm, "mid": v(-114.5, -21.22) * mm, "end": v(-113.91, -24.21) * mm});
            skLineSegment(sketch, "E33.17.3", {"start": v(-103.51, -16.4) * mm, "end": v(-115.02, -18.22) * mm});
            skArc(sketch, "E34.3.18.0", {"start": v(-101.23, -27.12) * mm, "mid": v(-100.49, -29.77) * mm, "end": v(-99.67, -32.39) * mm});
            skLineSegment(sketch, "E34.4.18.0", {"start": v(-110.76, -35.99) * mm, "end": v(-99.67, -32.39) * mm});
            skArc(sketch, "E34.7.18.0", {"start": v(-112.49, -30.14) * mm, "mid": v(-111.66, -33.08) * mm, "end": v(-110.76, -35.99) * mm});
            skLineSegment(sketch, "E34.11.18.0", {"start": v(-101.23, -27.12) * mm, "end": v(-112.49, -30.14) * mm});
            skArc(sketch, "E34.3.19.0", {"start": v(-97.84, -37.56) * mm, "mid": v(-96.83, -40.1) * mm, "end": v(-95.74, -42.63) * mm});
            skLineSegment(sketch, "E34.4.19.0", {"start": v(-106.39, -47.37) * mm, "end": v(-95.74, -42.63) * mm});
            skArc(sketch, "E34.7.19.0", {"start": v(-108.72, -41.73) * mm, "mid": v(-107.6, -44.57) * mm, "end": v(-106.39, -47.37) * mm});
            skLineSegment(sketch, "E34.11.19.0", {"start": v(-97.84, -37.56) * mm, "end": v(-108.72, -41.73) * mm});
            skArc(sketch, "E34.3.20.0", {"start": v(-93.38, -47.58) * mm, "mid": v(-92.1, -50) * mm, "end": v(-90.76, -52.4) * mm});
            skLineSegment(sketch, "E34.4.20.0", {"start": v(-100.85, -58.23) * mm, "end": v(-90.76, -52.4) * mm});
            skArc(sketch, "E34.7.20.0", {"start": v(-103.76, -52.87) * mm, "mid": v(-102.34, -55.57) * mm, "end": v(-100.85, -58.23) * mm});
            skLineSegment(sketch, "E34.11.20.0", {"start": v(-93.38, -47.58) * mm, "end": v(-103.76, -52.87) * mm});
            skArc(sketch, "E34.3.21.0", {"start": v(-87.9, -57.08) * mm, "mid": v(-86.37, -59.36) * mm, "end": v(-84.79, -61.6) * mm});
            skLineSegment(sketch, "E34.4.21.0", {"start": v(-94.22, -68.45) * mm, "end": v(-84.79, -61.6) * mm});
            skArc(sketch, "E34.7.21.0", {"start": v(-97.67, -63.43) * mm, "mid": v(-95.97, -65.96) * mm, "end": v(-94.22, -68.45) * mm});
            skLineSegment(sketch, "E34.11.21.0", {"start": v(-87.9, -57.08) * mm, "end": v(-97.67, -63.43) * mm});
            skArc(sketch, "E34.3.22.0", {"start": v(-81.45, -65.95) * mm, "mid": v(-79.7, -68.06) * mm, "end": v(-77.88, -70.13) * mm});
            skLineSegment(sketch, "E34.4.22.0", {"start": v(-86.54, -77.92) * mm, "end": v(-77.88, -70.13) * mm});
            skArc(sketch, "E34.7.22.0", {"start": v(-90.5, -73.29) * mm, "mid": v(-88.55, -75.63) * mm, "end": v(-86.54, -77.92) * mm});
            skLineSegment(sketch, "E34.11.22.0", {"start": v(-81.45, -65.95) * mm, "end": v(-90.5, -73.29) * mm});
            skArc(sketch, "E34.3.23.0", {"start": v(-74.1, -74.1) * mm, "mid": v(-72.14, -76.02) * mm, "end": v(-70.13, -77.88) * mm});
            skLineSegment(sketch, "E34.4.23.0", {"start": v(-77.92, -86.54) * mm, "end": v(-70.13, -77.88) * mm});
            skArc(sketch, "E34.7.23.0", {"start": v(-82.35, -82.35) * mm, "mid": v(-80.16, -84.47) * mm, "end": v(-77.92, -86.54) * mm});
            skLineSegment(sketch, "E34.11.23.0", {"start": v(-74.1, -74.1) * mm, "end": v(-82.35, -82.35) * mm});
            skArc(sketch, "E34.3.24.0", {"start": v(-65.95, -81.45) * mm, "mid": v(-63.8, -83.15) * mm, "end": v(-61.6, -84.79) * mm});
            skLineSegment(sketch, "E34.4.24.0", {"start": v(-68.45, -94.22) * mm, "end": v(-61.6, -84.79) * mm});
            skArc(sketch, "E34.7.24.0", {"start": v(-73.29, -90.5) * mm, "mid": v(-70.9, -92.4) * mm, "end": v(-68.45, -94.22) * mm});
            skLineSegment(sketch, "E34.11.24.0", {"start": v(-65.95, -81.45) * mm, "end": v(-73.29, -90.5) * mm});
            skArc(sketch, "E34.3.25.0", {"start": v(-57.08, -87.9) * mm, "mid": v(-54.76, -89.36) * mm, "end": v(-52.4, -90.76) * mm});
            skLineSegment(sketch, "E34.4.25.0", {"start": v(-58.23, -100.85) * mm, "end": v(-52.4, -90.76) * mm});
            skArc(sketch, "E34.7.25.0", {"start": v(-63.43, -97.67) * mm, "mid": v(-60.85, -99.3) * mm, "end": v(-58.23, -100.85) * mm});
            skLineSegment(sketch, "E34.11.25.0", {"start": v(-57.08, -87.9) * mm, "end": v(-63.43, -97.67) * mm});
            skArc(sketch, "E34.3.26.0", {"start": v(-47.58, -93.38) * mm, "mid": v(-45.12, -94.6) * mm, "end": v(-42.63, -95.74) * mm});
            skLineSegment(sketch, "E34.4.26.0", {"start": v(-47.37, -106.39) * mm, "end": v(-42.63, -95.74) * mm});
            skArc(sketch, "E34.7.26.0", {"start": v(-52.87, -103.76) * mm, "mid": v(-50.14, -105.11) * mm, "end": v(-47.37, -106.39) * mm});
            skLineSegment(sketch, "E34.11.26.0", {"start": v(-47.58, -93.38) * mm, "end": v(-52.87, -103.76) * mm});
            skArc(sketch, "E34.3.27.0", {"start": v(-37.56, -97.84) * mm, "mid": v(-34.98, -98.8) * mm, "end": v(-32.39, -99.67) * mm});
            skLineSegment(sketch, "E34.4.27.0", {"start": v(-35.99, -110.76) * mm, "end": v(-32.39, -99.67) * mm});
            skArc(sketch, "E34.7.27.0", {"start": v(-41.73, -108.72) * mm, "mid": v(-38.87, -109.78) * mm, "end": v(-35.99, -110.76) * mm});
            skLineSegment(sketch, "E34.11.27.0", {"start": v(-37.56, -97.84) * mm, "end": v(-41.73, -108.72) * mm});
            skArc(sketch, "E34.3.28.0", {"start": v(-27.12, -101.23) * mm, "mid": v(-24.47, -101.9) * mm, "end": v(-21.79, -102.51) * mm});
            skLineSegment(sketch, "E34.4.28.0", {"start": v(-24.21, -113.91) * mm, "end": v(-21.79, -102.51) * mm});
            skArc(sketch, "E34.7.28.0", {"start": v(-30.14, -112.49) * mm, "mid": v(-27.19, -113.24) * mm, "end": v(-24.21, -113.91) * mm});
            skLineSegment(sketch, "E34.11.28.0", {"start": v(-27.12, -101.23) * mm, "end": v(-30.14, -112.49) * mm});
            skArc(sketch, "E34.3.29.0", {"start": v(-16.4, -103.51) * mm, "mid": v(-13.68, -103.9) * mm, "end": v(-10.95, -104.23) * mm});
            skLineSegment(sketch, "E34.4.29.0", {"start": v(-12.17, -115.82) * mm, "end": v(-10.95, -104.23) * mm});
            skArc(sketch, "E34.7.29.0", {"start": v(-18.22, -115.02) * mm, "mid": v(-15.2, -115.46) * mm, "end": v(-12.17, -115.82) * mm});
            skLineSegment(sketch, "E34.11.29.0", {"start": v(-16.4, -103.51) * mm, "end": v(-18.22, -115.02) * mm});
            skArc(sketch, "E34.3.30.0", {"start": v(-5.48, -104.66) * mm, "mid": v(-2.74, -104.77) * mm, "end": v(0, -104.8) * mm});
            skLineSegment(sketch, "E34.4.30.0", {"start": v(0, -116.46) * mm, "end": v(0, -104.8) * mm});
            skArc(sketch, "E34.7.30.0", {"start": v(-6.1, -116.3) * mm, "mid": v(-3.05, -116.42) * mm, "end": v(0, -116.46) * mm});
            skLineSegment(sketch, "E34.11.30.0", {"start": v(-5.48, -104.66) * mm, "end": v(-6.1, -116.3) * mm});
            skArc(sketch, "E34.3.31.0", {"start": v(5.48, -104.66) * mm, "mid": v(8.22, -104.48) * mm, "end": v(10.95, -104.23) * mm});
            skLineSegment(sketch, "E34.4.31.0", {"start": v(12.17, -115.82) * mm, "end": v(10.95, -104.23) * mm});
            skArc(sketch, "E34.7.31.0", {"start": v(6.1, -116.3) * mm, "mid": v(9.14, -116.1) * mm, "end": v(12.17, -115.82) * mm});
            skLineSegment(sketch, "E34.11.31.0", {"start": v(5.48, -104.66) * mm, "end": v(6.1, -116.3) * mm});
            skArc(sketch, "E34.3.32.0", {"start": v(16.4, -103.51) * mm, "mid": v(19.1, -103.05) * mm, "end": v(21.79, -102.51) * mm});
            skLineSegment(sketch, "E34.4.32.0", {"start": v(24.21, -113.91) * mm, "end": v(21.79, -102.51) * mm});
            skArc(sketch, "E34.7.32.0", {"start": v(18.22, -115.02) * mm, "mid": v(21.22, -114.5) * mm, "end": v(24.21, -113.91) * mm});
            skLineSegment(sketch, "E34.11.32.0", {"start": v(16.4, -103.51) * mm, "end": v(18.22, -115.02) * mm});
            skArc(sketch, "E34.3.33.0", {"start": v(27.12, -101.23) * mm, "mid": v(29.77, -100.49) * mm, "end": v(32.39, -99.67) * mm});
            skLineSegment(sketch, "E34.4.33.0", {"start": v(35.99, -110.76) * mm, "end": v(32.39, -99.67) * mm});
            skArc(sketch, "E34.7.33.0", {"start": v(30.14, -112.49) * mm, "mid": v(33.08, -111.66) * mm, "end": v(35.99, -110.76) * mm});
            skLineSegment(sketch, "E34.11.33.0", {"start": v(27.12, -101.23) * mm, "end": v(30.14, -112.49) * mm});
            skArc(sketch, "E34.3.34.0", {"start": v(37.56, -97.84) * mm, "mid": v(40.1, -96.83) * mm, "end": v(42.63, -95.74) * mm});
            skLineSegment(sketch, "E34.4.34.0", {"start": v(47.37, -106.39) * mm, "end": v(42.63, -95.74) * mm});
            skArc(sketch, "E34.7.34.0", {"start": v(41.73, -108.72) * mm, "mid": v(44.57, -107.6) * mm, "end": v(47.37, -106.39) * mm});
            skLineSegment(sketch, "E34.11.34.0", {"start": v(37.56, -97.84) * mm, "end": v(41.73, -108.72) * mm});
            skArc(sketch, "E34.3.35.0", {"start": v(47.58, -93.38) * mm, "mid": v(50, -92.1) * mm, "end": v(52.4, -90.76) * mm});
            skLineSegment(sketch, "E34.4.35.0", {"start": v(58.23, -100.85) * mm, "end": v(52.4, -90.76) * mm});
            skArc(sketch, "E34.7.35.0", {"start": v(52.87, -103.76) * mm, "mid": v(55.57, -102.34) * mm, "end": v(58.23, -100.85) * mm});
            skLineSegment(sketch, "E34.11.35.0", {"start": v(47.58, -93.38) * mm, "end": v(52.87, -103.76) * mm});
            skArc(sketch, "E35.3.36.0", {"start": v(57.08, -87.9) * mm, "mid": v(59.36, -86.37) * mm, "end": v(61.6, -84.79) * mm});
            skLineSegment(sketch, "E35.4.36.0", {"start": v(68.45, -94.22) * mm, "end": v(61.6, -84.79) * mm});
            skArc(sketch, "E35.7.36.0", {"start": v(63.43, -97.67) * mm, "mid": v(65.96, -95.97) * mm, "end": v(68.45, -94.22) * mm});
            skLineSegment(sketch, "E35.11.36.0", {"start": v(57.08, -87.9) * mm, "end": v(63.43, -97.67) * mm});
            skArc(sketch, "E35.3.37.0", {"start": v(65.95, -81.45) * mm, "mid": v(68.06, -79.7) * mm, "end": v(70.13, -77.88) * mm});
            skLineSegment(sketch, "E35.4.37.0", {"start": v(77.92, -86.54) * mm, "end": v(70.13, -77.88) * mm});
            skArc(sketch, "E35.7.37.0", {"start": v(73.29, -90.5) * mm, "mid": v(75.63, -88.55) * mm, "end": v(77.92, -86.54) * mm});
            skLineSegment(sketch, "E35.11.37.0", {"start": v(65.95, -81.45) * mm, "end": v(73.29, -90.5) * mm});
            skArc(sketch, "E35.3.38.0", {"start": v(74.1, -74.1) * mm, "mid": v(76.02, -72.14) * mm, "end": v(77.88, -70.13) * mm});
            skLineSegment(sketch, "E35.4.38.0", {"start": v(86.54, -77.92) * mm, "end": v(77.88, -70.13) * mm});
            skArc(sketch, "E35.7.38.0", {"start": v(82.35, -82.35) * mm, "mid": v(84.47, -80.16) * mm, "end": v(86.54, -77.92) * mm});
            skLineSegment(sketch, "E35.11.38.0", {"start": v(74.1, -74.1) * mm, "end": v(82.35, -82.35) * mm});
            skArc(sketch, "E35.3.39.0", {"start": v(81.45, -65.95) * mm, "mid": v(83.15, -63.8) * mm, "end": v(84.79, -61.6) * mm});
            skLineSegment(sketch, "E35.4.39.0", {"start": v(94.22, -68.45) * mm, "end": v(84.79, -61.6) * mm});
            skArc(sketch, "E35.7.39.0", {"start": v(90.5, -73.29) * mm, "mid": v(92.4, -70.9) * mm, "end": v(94.22, -68.45) * mm});
            skLineSegment(sketch, "E35.11.39.0", {"start": v(81.45, -65.95) * mm, "end": v(90.5, -73.29) * mm});
            skArc(sketch, "E35.3.40.0", {"start": v(87.9, -57.08) * mm, "mid": v(89.36, -54.76) * mm, "end": v(90.76, -52.4) * mm});
            skLineSegment(sketch, "E35.4.40.0", {"start": v(100.85, -58.23) * mm, "end": v(90.76, -52.4) * mm});
            skArc(sketch, "E35.7.40.0", {"start": v(97.67, -63.43) * mm, "mid": v(99.3, -60.85) * mm, "end": v(100.85, -58.23) * mm});
            skLineSegment(sketch, "E35.11.40.0", {"start": v(87.9, -57.08) * mm, "end": v(97.67, -63.43) * mm});
            skArc(sketch, "E35.3.41.0", {"start": v(93.38, -47.58) * mm, "mid": v(94.6, -45.12) * mm, "end": v(95.74, -42.63) * mm});
            skLineSegment(sketch, "E35.4.41.0", {"start": v(106.39, -47.37) * mm, "end": v(95.74, -42.63) * mm});
            skArc(sketch, "E35.7.41.0", {"start": v(103.76, -52.87) * mm, "mid": v(105.11, -50.14) * mm, "end": v(106.39, -47.37) * mm});
            skLineSegment(sketch, "E35.11.41.0", {"start": v(93.38, -47.58) * mm, "end": v(103.76, -52.87) * mm});
            skArc(sketch, "E35.3.42.0", {"start": v(97.84, -37.56) * mm, "mid": v(98.8, -34.98) * mm, "end": v(99.67, -32.39) * mm});
            skLineSegment(sketch, "E35.4.42.0", {"start": v(110.76, -35.99) * mm, "end": v(99.67, -32.39) * mm});
            skArc(sketch, "E35.7.42.0", {"start": v(108.72, -41.73) * mm, "mid": v(109.78, -38.87) * mm, "end": v(110.76, -35.99) * mm});
            skLineSegment(sketch, "E35.11.42.0", {"start": v(97.84, -37.56) * mm, "end": v(108.72, -41.73) * mm});
            skArc(sketch, "E35.3.43.0", {"start": v(101.23, -27.12) * mm, "mid": v(101.9, -24.47) * mm, "end": v(102.51, -21.79) * mm});
            skLineSegment(sketch, "E35.4.43.0", {"start": v(113.91, -24.21) * mm, "end": v(102.51, -21.79) * mm});
            skArc(sketch, "E35.7.43.0", {"start": v(112.49, -30.14) * mm, "mid": v(113.24, -27.19) * mm, "end": v(113.91, -24.21) * mm});
            skLineSegment(sketch, "E35.11.43.0", {"start": v(101.23, -27.12) * mm, "end": v(112.49, -30.14) * mm});
            skArc(sketch, "E35.3.44.0", {"start": v(103.51, -16.4) * mm, "mid": v(103.9, -13.68) * mm, "end": v(104.23, -10.95) * mm});
            skLineSegment(sketch, "E35.4.44.0", {"start": v(115.82, -12.17) * mm, "end": v(104.23, -10.95) * mm});
            skArc(sketch, "E35.7.44.0", {"start": v(115.02, -18.22) * mm, "mid": v(115.46, -15.2) * mm, "end": v(115.82, -12.17) * mm});
            skLineSegment(sketch, "E35.11.44.0", {"start": v(103.51, -16.4) * mm, "end": v(115.02, -18.22) * mm});
            skArc(sketch, "E36.3.45.0", {"start": v(104.66, -5.48) * mm, "mid": v(104.77, -2.74) * mm, "end": v(104.8, 0) * mm});
            skLineSegment(sketch, "E36.4.45.0", {"start": v(116.46, 0) * mm, "end": v(104.8, 0) * mm});
            skArc(sketch, "E36.7.45.0", {"start": v(116.3, -6.1) * mm, "mid": v(116.42, -3.05) * mm, "end": v(116.46, 0) * mm});
            skLineSegment(sketch, "E36.11.45.0", {"start": v(104.66, -5.48) * mm, "end": v(116.3, -6.1) * mm});
            skArc(sketch, "E36.3.46.0", {"start": v(104.66, 5.48) * mm, "mid": v(104.48, 8.22) * mm, "end": v(104.23, 10.95) * mm});
            skLineSegment(sketch, "E36.4.46.0", {"start": v(115.82, 12.17) * mm, "end": v(104.23, 10.95) * mm});
            skArc(sketch, "E36.7.46.0", {"start": v(116.3, 6.1) * mm, "mid": v(116.1, 9.14) * mm, "end": v(115.82, 12.17) * mm});
            skLineSegment(sketch, "E36.11.46.0", {"start": v(104.66, 5.48) * mm, "end": v(116.3, 6.1) * mm});
            skArc(sketch, "E36.3.47.0", {"start": v(103.51, 16.4) * mm, "mid": v(103.05, 19.1) * mm, "end": v(102.51, 21.79) * mm});
            skLineSegment(sketch, "E36.4.47.0", {"start": v(113.91, 24.21) * mm, "end": v(102.51, 21.79) * mm});
            skArc(sketch, "E36.7.47.0", {"start": v(115.02, 18.22) * mm, "mid": v(114.5, 21.22) * mm, "end": v(113.91, 24.21) * mm});
            skLineSegment(sketch, "E36.11.47.0", {"start": v(103.51, 16.4) * mm, "end": v(115.02, 18.22) * mm});
            skArc(sketch, "E36.3.48.0", {"start": v(101.23, 27.12) * mm, "mid": v(100.49, 29.77) * mm, "end": v(99.67, 32.39) * mm});
            skLineSegment(sketch, "E36.4.48.0", {"start": v(110.76, 35.99) * mm, "end": v(99.67, 32.39) * mm});
            skArc(sketch, "E36.7.48.0", {"start": v(112.49, 30.14) * mm, "mid": v(111.66, 33.08) * mm, "end": v(110.76, 35.99) * mm});
            skLineSegment(sketch, "E36.11.48.0", {"start": v(101.23, 27.12) * mm, "end": v(112.49, 30.14) * mm});
            skArc(sketch, "E36.3.49.0", {"start": v(97.84, 37.56) * mm, "mid": v(96.83, 40.1) * mm, "end": v(95.74, 42.63) * mm});
            skLineSegment(sketch, "E36.4.49.0", {"start": v(106.39, 47.37) * mm, "end": v(95.74, 42.63) * mm});
            skArc(sketch, "E36.7.49.0", {"start": v(108.72, 41.73) * mm, "mid": v(107.6, 44.57) * mm, "end": v(106.39, 47.37) * mm});
            skLineSegment(sketch, "E36.11.49.0", {"start": v(97.84, 37.56) * mm, "end": v(108.72, 41.73) * mm});
            skArc(sketch, "E36.3.50.0", {"start": v(93.38, 47.58) * mm, "mid": v(92.1, 50) * mm, "end": v(90.76, 52.4) * mm});
            skLineSegment(sketch, "E36.4.50.0", {"start": v(100.85, 58.23) * mm, "end": v(90.76, 52.4) * mm});
            skArc(sketch, "E36.7.50.0", {"start": v(103.76, 52.87) * mm, "mid": v(102.34, 55.57) * mm, "end": v(100.85, 58.23) * mm});
            skLineSegment(sketch, "E36.11.50.0", {"start": v(93.38, 47.58) * mm, "end": v(103.76, 52.87) * mm});
            skArc(sketch, "E36.3.51.0", {"start": v(87.9, 57.08) * mm, "mid": v(86.37, 59.36) * mm, "end": v(84.79, 61.6) * mm});
            skLineSegment(sketch, "E36.4.51.0", {"start": v(94.22, 68.45) * mm, "end": v(84.79, 61.6) * mm});
            skArc(sketch, "E36.7.51.0", {"start": v(97.67, 63.43) * mm, "mid": v(95.97, 65.96) * mm, "end": v(94.22, 68.45) * mm});
            skLineSegment(sketch, "E36.11.51.0", {"start": v(87.9, 57.08) * mm, "end": v(97.67, 63.43) * mm});
            skArc(sketch, "E36.3.52.0", {"start": v(81.45, 65.95) * mm, "mid": v(79.7, 68.06) * mm, "end": v(77.88, 70.13) * mm});
            skLineSegment(sketch, "E36.4.52.0", {"start": v(86.54, 77.92) * mm, "end": v(77.88, 70.13) * mm});
            skArc(sketch, "E36.7.52.0", {"start": v(90.5, 73.29) * mm, "mid": v(88.55, 75.63) * mm, "end": v(86.54, 77.92) * mm});
            skLineSegment(sketch, "E36.11.52.0", {"start": v(81.45, 65.95) * mm, "end": v(90.5, 73.29) * mm});
            skArc(sketch, "E36.3.53.0", {"start": v(74.1, 74.1) * mm, "mid": v(72.14, 76.02) * mm, "end": v(70.13, 77.88) * mm});
            skLineSegment(sketch, "E36.4.53.0", {"start": v(77.92, 86.54) * mm, "end": v(70.13, 77.88) * mm});
            skArc(sketch, "E36.7.53.0", {"start": v(82.35, 82.35) * mm, "mid": v(80.16, 84.47) * mm, "end": v(77.92, 86.54) * mm});
            skLineSegment(sketch, "E36.11.53.0", {"start": v(74.1, 74.1) * mm, "end": v(82.35, 82.35) * mm});
            skArc(sketch, "E36.3.54.0", {"start": v(65.95, 81.45) * mm, "mid": v(63.8, 83.15) * mm, "end": v(61.6, 84.79) * mm});
            skLineSegment(sketch, "E36.4.54.0", {"start": v(68.45, 94.22) * mm, "end": v(61.6, 84.79) * mm});
            skArc(sketch, "E36.7.54.0", {"start": v(73.29, 90.5) * mm, "mid": v(70.9, 92.4) * mm, "end": v(68.45, 94.22) * mm});
            skLineSegment(sketch, "E36.11.54.0", {"start": v(65.95, 81.45) * mm, "end": v(73.29, 90.5) * mm});
            skArc(sketch, "E36.3.55.0", {"start": v(57.08, 87.9) * mm, "mid": v(54.76, 89.36) * mm, "end": v(52.4, 90.76) * mm});
            skLineSegment(sketch, "E36.4.55.0", {"start": v(58.23, 100.85) * mm, "end": v(52.4, 90.76) * mm});
            skArc(sketch, "E36.7.55.0", {"start": v(63.43, 97.67) * mm, "mid": v(60.85, 99.3) * mm, "end": v(58.23, 100.85) * mm});
            skLineSegment(sketch, "E36.11.55.0", {"start": v(57.08, 87.9) * mm, "end": v(63.43, 97.67) * mm});
            skArc(sketch, "E36.3.56.0", {"start": v(47.58, 93.38) * mm, "mid": v(45.12, 94.6) * mm, "end": v(42.63, 95.74) * mm});
            skLineSegment(sketch, "E36.4.56.0", {"start": v(47.37, 106.39) * mm, "end": v(42.63, 95.74) * mm});
            skArc(sketch, "E36.7.56.0", {"start": v(52.87, 103.76) * mm, "mid": v(50.14, 105.11) * mm, "end": v(47.37, 106.39) * mm});
            skLineSegment(sketch, "E36.11.56.0", {"start": v(47.58, 93.38) * mm, "end": v(52.87, 103.76) * mm});
            skArc(sketch, "E36.3.57.0", {"start": v(37.56, 97.84) * mm, "mid": v(34.98, 98.8) * mm, "end": v(32.39, 99.67) * mm});
            skLineSegment(sketch, "E36.4.57.0", {"start": v(35.99, 110.76) * mm, "end": v(32.39, 99.67) * mm});
            skArc(sketch, "E36.7.57.0", {"start": v(41.73, 108.72) * mm, "mid": v(38.87, 109.78) * mm, "end": v(35.99, 110.76) * mm});
            skLineSegment(sketch, "E36.11.57.0", {"start": v(37.56, 97.84) * mm, "end": v(41.73, 108.72) * mm});
            skArc(sketch, "E36.3.58.0", {"start": v(27.12, 101.23) * mm, "mid": v(24.47, 101.9) * mm, "end": v(21.79, 102.51) * mm});
            skLineSegment(sketch, "E36.4.58.0", {"start": v(24.21, 113.91) * mm, "end": v(21.79, 102.51) * mm});
            skArc(sketch, "E36.7.58.0", {"start": v(30.14, 112.49) * mm, "mid": v(27.19, 113.24) * mm, "end": v(24.21, 113.91) * mm});
            skLineSegment(sketch, "E36.11.58.0", {"start": v(27.12, 101.23) * mm, "end": v(30.14, 112.49) * mm});
            skArc(sketch, "E36.3.59.0", {"start": v(16.4, 103.51) * mm, "mid": v(13.68, 103.9) * mm, "end": v(10.95, 104.23) * mm});
            skLineSegment(sketch, "E36.4.59.0", {"start": v(12.17, 115.82) * mm, "end": v(10.95, 104.23) * mm});
            skArc(sketch, "E36.7.59.0", {"start": v(18.22, 115.02) * mm, "mid": v(15.2, 115.46) * mm, "end": v(12.17, 115.82) * mm});
            skLineSegment(sketch, "E36.11.59.0", {"start": v(16.4, 103.51) * mm, "end": v(18.22, 115.02) * mm});
            skSolve(sketch);
        }
        {
            var Q0;
            Q0=qSketchRegion(id+"F4",true);
            extrude(context, id + "F5", {"entities" : qUnion([Q0]), "operationType" : NewBodyOperationType.REMOVE, "oppositeDirection" : true, "depth" : 25 * mm, "offsetDistance" : 25 * mm});
        }
    });
